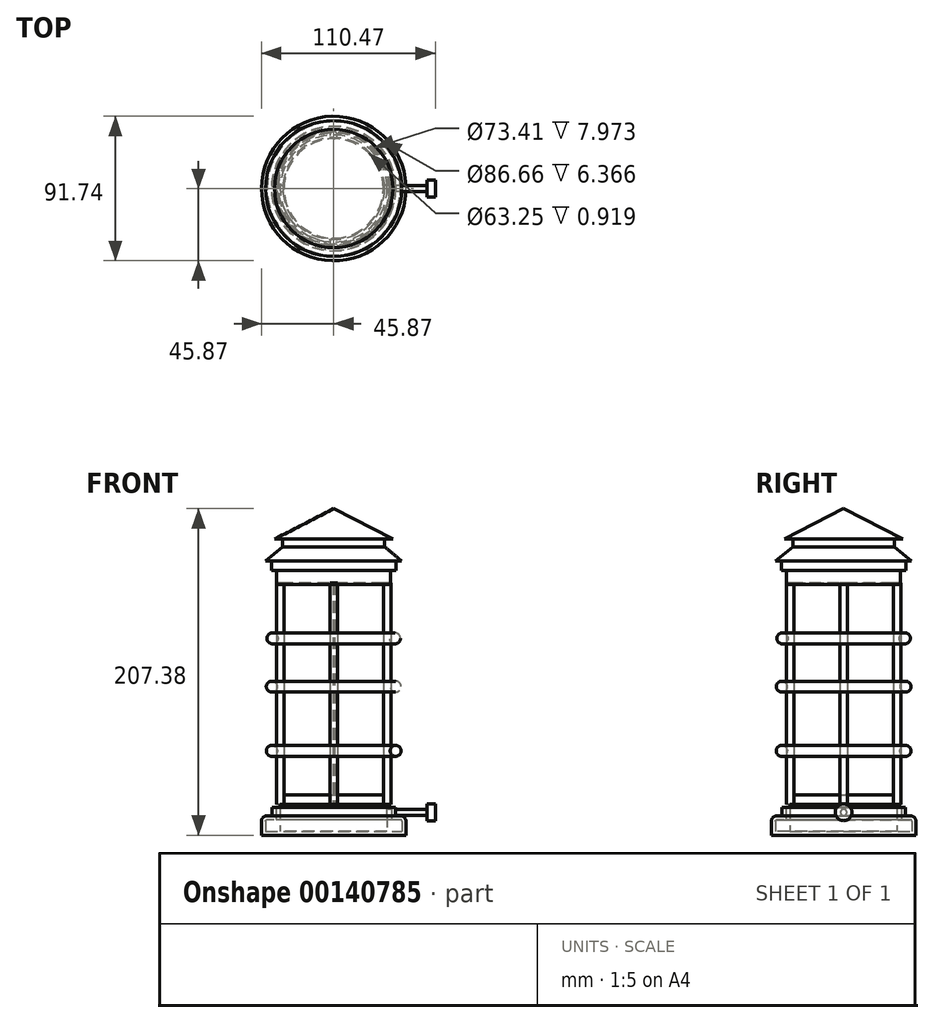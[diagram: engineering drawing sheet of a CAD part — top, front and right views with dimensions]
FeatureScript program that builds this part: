
annotation { "Feature Type Name" : "Feature", "Feature Type Description" : "" }
export const myFeature = defineFeature(function(context is Context, id is Id, definition is map)
    precondition{}
    {
        {
            var Q0;
            Q0=qCreatedBy(makeId("Front.planeOp"),FACE);
            var sketch = newSketch(context, id + "F0", { "sketchPlane" : qUnion([Q0])});
            skLineSegment(sketch, "E0", {"start": v(0, -64.78) * mm, "end": v(-52.83, -64.78) * mm});
            skLineSegment(sketch, "E1", {"start": v(-52.83, -64.78) * mm, "end": v(-45.18, -57.68) * mm});
            skLineSegment(sketch, "E2", {"start": v(-45.18, -57.68) * mm, "end": v(-45.18, -42.8) * mm});
            skLineSegment(sketch, "E3", {"start": v(-45.18, -42.8) * mm, "end": v(-47.57, -42.8) * mm});
            skLineSegment(sketch, "E4", {"start": v(-47.57, -42.8) * mm, "end": v(-47.57, -40.94) * mm});
            skLineSegment(sketch, "E5", {"start": v(-47.57, -40.94) * mm, "end": v(0, -40.94) * mm});
            skLineSegment(sketch, "E6", {"start": v(0, -40.94) * mm, "end": v(0, -64.78) * mm, "construction": true});
            skSolve(sketch);
        }
        {
            var Q0;
            Q0=sQuery(id+"F0.wireOp",EDGE,"E5");
            var Q1;
            Q1=sQuery(id+"F0.wireOp",EDGE,"E4");
            var Q2;
            Q2=sQuery(id+"F0.wireOp",EDGE,"E3");
            var Q3;
            Q3=sQuery(id+"F0.wireOp",EDGE,"E2");
            var Q4;
            Q4=sQuery(id+"F0.wireOp",EDGE,"E1");
            var Q5;
            Q5=sQuery(id+"F0.wireOp",EDGE,"E0");
            var Q6;
            Q6=sQuery(id+"F0.wireOp",EDGE,"E6");
            revolve(context, id + "F1", {"bodyType" : ToolBodyType.SURFACE, "surfaceEntities" : qUnion([Q0, Q1, Q2, Q3, Q4, Q5]), "axis" : qUnion([Q6]), "revolveType" : RevolveType.FULL});
        }
        {
            var Q0;
            Q0=makeQuery(id+"F1.opRevolve","SWEPT_FACE",FACE,{"disambiguationData":[OSD([sQuery(id+"F0.wireOp",EDGE,"E5")])]});
            var sketch = newSketch(context, id + "F2", { "sketchPlane" : qUnion([Q0])});
            skCircle(sketch, "E7", {"center": v(0, 0) * mm, "radius": 45.87 * mm});
            skSolve(sketch);
        }
        {
            var Q0;
            Q0=makeQuery(id+"F2.imprint","IMPRINT",FACE,{"disambiguationData":[TD([[makeQuery(id+"F2.imprint","IMPRINT",EDGE,{"derivedFrom":sQuery(id+"F2.wireOp",EDGE,"E7")}),1.0]])]});
            extrude(context, id + "F3", {"entities" : qUnion([Q0]), "depth" : 12.23 * mm});
        }
        {
            var Q0;
            Q0=makeQuery(id+"F3.opExtrude","CAP_EDGE",EDGE,{"disambiguationData":[OSD([sQuery(id+"F2.wireOp",EDGE,"E7")])],"isStart":false});
            fillet(context, id + "F4", {"entities" : qUnion([Q0]), "radius" : 3.32 * mm, "tangentPropagation" : true, "allowEdgeOverflow" : false});
        }
        {
            var Q0;
            Q0=makeQuery(id+"F3.opExtrude","CAP_FACE",FACE,{"disambiguationData":[OSD([sQuery(id+"F2.wireOp",EDGE,"E7")])],"isStart":false});
            var sketch = newSketch(context, id + "F5", { "sketchPlane" : qUnion([Q0])});
            skCircle(sketch, "E8", {"center": v(0, 0) * mm, "radius": 39.24 * mm});
            skSolve(sketch);
        }
        {
            var Q0;
            Q0=makeQuery(id+"F5.imprint","IMPRINT",FACE,{"disambiguationData":[TD([[makeQuery(id+"F5.imprint","IMPRINT",EDGE,{"derivedFrom":sQuery(id+"F5.wireOp",EDGE,"E8")}),1.0]])]});
            extrude(context, id + "F6", {"entities" : qUnion([Q0]), "operationType" : NewBodyOperationType.ADD, "depth" : 5.43 * mm});
        }
        {
            var Q0;
            Q0=makeQuery(id+"F6.opExtrude","CAP_FACE",FACE,{"disambiguationData":[OSD([sQuery(id+"F5.wireOp",EDGE,"E8")])],"isStart":false});
            shell(context, id + "F7", {"entities" : qUnion([Q0]), "thickness" : 2.54 * mm});
        }
        {
            var Q0;
            {var subQ0=sQuery(id+"F2.wireOp",EDGE,"E7");Q0=makeQuery(id+"F7.opShell","OFFSET_FACE",FACE,{"disambiguationData":[OSD([subQ0]),TDD([makeQuery(id+"F3.opExtrude","CAP_FACE",FACE,{"disambiguationData":[OSD([subQ0])],"isStart":true})])]});}
            var sketch = newSketch(context, id + "F8", { "sketchPlane" : qUnion([Q0])});
            skCircle(sketch, "E9", {"center": v(0, 0) * mm, "radius": 33.95 * mm});
            skSolve(sketch);
        }
        {
            var Q0;
            Q0 = qSketchRegion(id + "F8", true);
            extrude(context, id + "F9", {"entities" : qUnion([Q0]), "operationType" : NewBodyOperationType.ADD, "depth" : 17.16 * mm});
        }
        {
            var Q0;
            Q0=makeQuery(id+"F9.opExtrude","CAP_FACE",FACE,{"disambiguationData":[OSD([sQuery(id+"F8.wireOp",EDGE,"E9")])],"isStart":false});
            var sketch = newSketch(context, id + "F10", { "sketchPlane" : qUnion([Q0])});
            skCircle(sketch, "E10", {"center": v(0, 0) * mm, "radius": 31.65 * mm});
            skSolve(sketch);
        }
        {
            var Q0;
            Q0 = qSketchRegion(id + "F10", true);
            extrude(context, id + "F11", {"entities" : qUnion([Q0]), "operationType" : NewBodyOperationType.ADD, "depth" : 5.86 * mm});
        }
        {
            var Q0;
            Q0=makeQuery(id+"F9.opExtrude","CAP_FACE",FACE,{"disambiguationData":[OSD([sQuery(id+"F8.wireOp",EDGE,"E9")])],"isStart":false});
            var sketch = newSketch(context, id + "F12", { "sketchPlane" : qUnion([Q0])});
            skCircle(sketch, "E11", {"center": v(33.95, 0) * mm, "radius": 2.3 * mm});
            skCircle(sketch, "E12", {"center": v(-33.95, 0) * mm, "radius": 2.3 * mm});
            skCircle(sketch, "E13", {"center": v(0, 33.95) * mm, "radius": 2.3 * mm});
            skCircle(sketch, "E14", {"center": v(0, -33.95) * mm, "radius": 2.34 * mm});
            skSolve(sketch);
        }
        {
            var Q0;
            {var subQ0=sQuery(id+"F12.wireOp",EDGE,"E11");var subQ1=makeQuery(id+"F9.opExtrude","CAP_EDGE",EDGE,{"disambiguationData":[OSD([sQuery(id+"F8.wireOp",EDGE,"E9")])],"isStart":false});var subQ2=makeQuery(id+"F12.imprint","INTERSECT",VERTEX,{"disambiguationData":[OD(0.0)],"derivedFrom":[subQ1,subQ0]});Q0=makeQuery(id+"F12.imprint","IMPRINT",FACE,{"disambiguationData":[TD([[makeQuery(id+"F12.imprint","IMPRINT",EDGE,{"disambiguationData":[TD([[subQ2,1.0]])],"derivedFrom":subQ0}),1.0]])]});}
            var Q1;
            {var subQ0=sQuery(id+"F12.wireOp",EDGE,"E12");var subQ1=makeQuery(id+"F9.opExtrude","CAP_EDGE",EDGE,{"disambiguationData":[OSD([sQuery(id+"F8.wireOp",EDGE,"E9")])],"isStart":false});var subQ2=makeQuery(id+"F12.imprint","INTERSECT",VERTEX,{"disambiguationData":[OD(0.0)],"derivedFrom":[subQ1,subQ0]});Q1=makeQuery(id+"F12.imprint","IMPRINT",FACE,{"disambiguationData":[TD([[makeQuery(id+"F12.imprint","IMPRINT",EDGE,{"disambiguationData":[TD([[subQ2,1.0]])],"derivedFrom":subQ0}),1.0]])]});}
            var Q2;
            {var subQ0=sQuery(id+"F12.wireOp",EDGE,"E13");var subQ1=makeQuery(id+"F9.opExtrude","CAP_EDGE",EDGE,{"disambiguationData":[OSD([sQuery(id+"F8.wireOp",EDGE,"E9")])],"isStart":false});var subQ2=makeQuery(id+"F12.imprint","INTERSECT",VERTEX,{"disambiguationData":[OD(0.0)],"derivedFrom":[subQ1,subQ0]});Q2=makeQuery(id+"F12.imprint","IMPRINT",FACE,{"disambiguationData":[TD([[makeQuery(id+"F12.imprint","IMPRINT",EDGE,{"disambiguationData":[TD([[subQ2,1.0]])],"derivedFrom":subQ0}),1.0]])]});}
            var Q3;
            {var subQ0=sQuery(id+"F12.wireOp",EDGE,"E13");var subQ1=makeQuery(id+"F9.opExtrude","CAP_EDGE",EDGE,{"disambiguationData":[OSD([sQuery(id+"F8.wireOp",EDGE,"E9")])],"isStart":false});var subQ2=makeQuery(id+"F12.imprint","INTERSECT",VERTEX,{"disambiguationData":[OD(0.0)],"derivedFrom":[subQ1,subQ0]});Q3=makeQuery(id+"F12.imprint","IMPRINT",FACE,{"disambiguationData":[TD([[makeQuery(id+"F12.imprint","IMPRINT",EDGE,{"disambiguationData":[TD([[subQ2,-1.0]])],"derivedFrom":subQ0}),1.0]])]});}
            var Q4;
            {var subQ0=sQuery(id+"F12.wireOp",EDGE,"E12");var subQ1=makeQuery(id+"F9.opExtrude","CAP_EDGE",EDGE,{"disambiguationData":[OSD([sQuery(id+"F8.wireOp",EDGE,"E9")])],"isStart":false});var subQ2=makeQuery(id+"F12.imprint","INTERSECT",VERTEX,{"disambiguationData":[OD(0.0)],"derivedFrom":[subQ1,subQ0]});Q4=makeQuery(id+"F12.imprint","IMPRINT",FACE,{"disambiguationData":[TD([[makeQuery(id+"F12.imprint","IMPRINT",EDGE,{"disambiguationData":[TD([[subQ2,-1.0]])],"derivedFrom":subQ0}),1.0]])]});}
            var Q5;
            {var subQ0=sQuery(id+"F12.wireOp",EDGE,"E11");var subQ1=makeQuery(id+"F9.opExtrude","CAP_EDGE",EDGE,{"disambiguationData":[OSD([sQuery(id+"F8.wireOp",EDGE,"E9")])],"isStart":false});var subQ2=makeQuery(id+"F12.imprint","INTERSECT",VERTEX,{"disambiguationData":[OD(0.0)],"derivedFrom":[subQ1,subQ0]});Q5=makeQuery(id+"F12.imprint","IMPRINT",FACE,{"disambiguationData":[TD([[makeQuery(id+"F12.imprint","IMPRINT",EDGE,{"disambiguationData":[TD([[subQ2,-1.0]])],"derivedFrom":subQ0}),1.0]])]});}
            var Q6;
            {var subQ0=sQuery(id+"F12.wireOp",EDGE,"E14");var subQ1=makeQuery(id+"F9.opExtrude","CAP_EDGE",EDGE,{"disambiguationData":[OSD([sQuery(id+"F8.wireOp",EDGE,"E9")])],"isStart":false});var subQ2=makeQuery(id+"F12.imprint","INTERSECT",VERTEX,{"disambiguationData":[OD(0.0)],"derivedFrom":[subQ1,subQ0]});Q6=makeQuery(id+"F12.imprint","IMPRINT",FACE,{"disambiguationData":[TD([[makeQuery(id+"F12.imprint","IMPRINT",EDGE,{"disambiguationData":[TD([[subQ2,-1.0]])],"derivedFrom":subQ0}),1.0]])]});}
            var Q7;
            {var subQ0=sQuery(id+"F12.wireOp",EDGE,"E14");var subQ1=makeQuery(id+"F9.opExtrude","CAP_EDGE",EDGE,{"disambiguationData":[OSD([sQuery(id+"F8.wireOp",EDGE,"E9")])],"isStart":false});var subQ2=makeQuery(id+"F12.imprint","INTERSECT",VERTEX,{"disambiguationData":[OD(0.0)],"derivedFrom":[subQ1,subQ0]});Q7=makeQuery(id+"F12.imprint","IMPRINT",FACE,{"disambiguationData":[TD([[makeQuery(id+"F12.imprint","IMPRINT",EDGE,{"disambiguationData":[TD([[subQ2,1.0]])],"derivedFrom":subQ0}),1.0]])]});}
            extrude(context, id + "F13", {"entities" : qUnion([Q0, Q1, Q2, Q3, Q4, Q5, Q6, Q7]), "depth" : 140.45 * mm});
        }
        {
            var Q0;
            Q0=makeQuery(id+"F11.opExtrude","CAP_FACE",FACE,{"disambiguationData":[OSD([sQuery(id+"F10.wireOp",EDGE,"E10")])],"isStart":false});
            extrude(context, id + "F14", {"entities" : qUnion([Q0]), "depth" : 134.56 * mm});
        }
        {
            var Q0;
            Q0=makeQuery(id+"F14.opExtrude","CAP_FACE",FACE,{"disambiguationData":[OSD([sQuery(id+"F10.wireOp",EDGE,"E10")])],"isStart":false});
            shell(context, id + "F15", {"entities" : qUnion([Q0]), "thickness" : 0.03 * mm});
        }
        {
            var Q0;
            {var subQ0=sQuery(id+"F10.wireOp",EDGE,"E10");Q0=makeQuery(id+"F15.opShell","OFFSET_FACE",FACE,{"disambiguationData":[OSD([subQ0]),TDD([makeQuery(id+"F14.opExtrude","CAP_FACE",FACE,{"disambiguationData":[OSD([subQ0])],"isStart":true})])]});}
            extrude(context, id + "F16", {"entities" : qUnion([Q0]), "operationType" : NewBodyOperationType.ADD, "depth" : 133.61 * mm});
        }
        {
            var Q0;
            Q0=makeQuery(id+"F16.opExtrude","CAP_FACE",FACE,{"disambiguationData":[OSD([sQuery(id+"F10.wireOp",EDGE,"E10")])],"isStart":false});
            var sketch = newSketch(context, id + "F17", { "sketchPlane" : qUnion([Q0])});
            skCircle(sketch, "E15", {"center": v(0, 0) * mm, "radius": 36.18 * mm});
            skSolve(sketch);
        }
        {
            var Q0;
            Q0 = qSketchRegion(id + "F17", true);
            extrude(context, id + "F18", {"entities" : qUnion([Q0]), "depth" : 8.96 * mm});
        }
        {
            var Q0;
            Q0=makeQuery(id+"F18.opExtrude","CAP_FACE",FACE,{"disambiguationData":[OSD([sQuery(id+"F17.wireOp",EDGE,"E15")])],"isStart":false});
            var sketch = newSketch(context, id + "F19", { "sketchPlane" : qUnion([Q0])});
            skCircle(sketch, "E16", {"center": v(0, 0) * mm, "radius": 39.6 * mm});
            skSolve(sketch);
        }
        {
            var Q0;
            Q0=makeQuery(id+"F19.imprint","IMPRINT",FACE,{"disambiguationData":[TD([[makeQuery(id+"F19.imprint","IMPRINT",EDGE,{"derivedFrom":sQuery(id+"F19.wireOp",EDGE,"E16")}),1.0]])]});
            var Q1;
            Q1=makeQuery(id+"F19.imprint","IMPRINT",FACE,{"disambiguationData":[TD([[makeQuery(id+"F19.imprint","IMPRINT",EDGE,{"derivedFrom":makeQuery(id+"F18.opExtrude","CAP_EDGE",EDGE,{"disambiguationData":[OSD([sQuery(id+"F17.wireOp",EDGE,"E15")])],"isStart":false})}),1.0]])]});
            extrude(context, id + "F20", {"entities" : qUnion([Q0, Q1]), "operationType" : NewBodyOperationType.ADD, "depth" : 6.14 * mm});
        }
        {
            var Q0;
            Q0=makeQuery(id+"F20.opExtrude","CAP_FACE",FACE,{"disambiguationData":[OSD([sQuery(id+"F19.wireOp",EDGE,"E16")])],"isStart":false});
            var sketch = newSketch(context, id + "F21", { "sketchPlane" : qUnion([Q0])});
            skSolve(sketch);
        }
        {
            var Q0;
            Q0=makeQuery(id+"F21.imprint","IMPRINT",FACE,{"disambiguationData":[TD([[makeQuery(id+"F21.imprint","IMPRINT",EDGE,{"derivedFrom":makeQuery(id+"F20.opExtrude","CAP_EDGE",EDGE,{"disambiguationData":[OSD([sQuery(id+"F19.wireOp",EDGE,"E16")])],"isStart":false})}),1.0]])]});
            var sketch = newSketch(context, id + "F22", { "sketchPlane" : qUnion([Q0])});
            skSolve(sketch);
        }
        {
            var Q0;
            Q0=makeQuery(id+"F22.imprint","IMPRINT",FACE,{"disambiguationData":[TD([[makeQuery(id+"F22.imprint","IMPRINT",EDGE,{"derivedFrom":makeQuery(id+"F21.imprint","IMPRINT",EDGE,{"derivedFrom":makeQuery(id+"F20.opExtrude","CAP_EDGE",EDGE,{"disambiguationData":[OSD([sQuery(id+"F19.wireOp",EDGE,"E16")])],"isStart":false})})}),1.0]])]});
            var sketch = newSketch(context, id + "F23", { "sketchPlane" : qUnion([Q0])});
            skCircle(sketch, "E17", {"center": v(0, 0) * mm, "radius": 5.35 * mm});
            skSolve(sketch);
        }
        {
            var Q0;
            Q0=makeQuery(id+"F23.imprint","IMPRINT",FACE,{"disambiguationData":[TD([[makeQuery(id+"F23.imprint","IMPRINT",EDGE,{"derivedFrom":sQuery(id+"F23.wireOp",EDGE,"E17")}),1.0]])]});
            extrude(context, id + "F24", {"entities" : qUnion([Q0]), "operationType" : NewBodyOperationType.ADD, "depth" : 28.78 * mm});
        }
        {
            var Q0;
            Q0=qCreatedBy(makeId("Front.planeOp"),FACE);
            var sketch = newSketch(context, id + "F25", { "sketchPlane" : qUnion([Q0])});
            skLineSegment(sketch, "E18", {"start": v(0, 148) * mm, "end": v(0, 133.15) * mm});
            skLineSegment(sketch, "E19", {"start": v(0, 133.15) * mm, "end": v(43.2, 133.15) * mm});
            skLineSegment(sketch, "E20", {"start": v(43.2, 133.15) * mm, "end": v(32.35, 142.24) * mm});
            skLineSegment(sketch, "E21", {"start": v(32.35, 142.24) * mm, "end": v(32.35, 147.08) * mm});
            skLineSegment(sketch, "E22", {"start": v(32.35, 147.08) * mm, "end": v(37.62, 147.08) * mm});
            skLineSegment(sketch, "E23", {"start": v(37.62, 147.08) * mm, "end": v(0, 166.44) * mm});
            skLineSegment(sketch, "E24", {"start": v(0, 166.44) * mm, "end": v(0, 148) * mm});
            skSolve(sketch);
        }
        {
            var Q0;
            Q0=makeQuery(id+"F25.imprint","IMPRINT",FACE,{"disambiguationData":[TD([[makeQuery(id+"F25.imprint","IMPRINT",EDGE,{"derivedFrom":sQuery(id+"F25.wireOp",EDGE,"E18")}),1.0]])]});
            var Q1;
            Q1=sQuery(id+"F25.wireOp",EDGE,"E24");
            revolve(context, id + "F26", {"operationType" : NewBodyOperationType.ADD, "entities" : qUnion([Q0]), "axis" : qUnion([Q1]), "revolveType" : RevolveType.FULL});
        }
        {
            var Q0;
            Q0=qCreatedBy(makeId("Right.planeOp"),FACE);
            var sketch = newSketch(context, id + "F27", { "sketchPlane" : qUnion([Q0])});
            skCircle(sketch, "E25", {"center": v(-39.38, 53.45) * mm, "radius": 3.44 * mm});
            skCircle(sketch, "E26", {"center": v(-39.3, 12.6) * mm, "radius": 3.5 * mm});
            skCircle(sketch, "E27", {"center": v(-38.89, 84.08) * mm, "radius": 3.5 * mm});
            skSolve(sketch);
        }
        {
            var Q0;
            Q0=sQuery(id+"F27.wireOp",EDGE,"E25");
            var Q1;
            Q1=makeQuery(id+"F14.opExtrude","SWEPT_FACE",FACE,{"disambiguationData":[OSD([sQuery(id+"F10.wireOp",EDGE,"E10")])]});
            revolve(context, id + "F28", {"bodyType" : ToolBodyType.SURFACE, "surfaceEntities" : qUnion([Q0]), "axis" : qUnion([Q1]), "revolveType" : RevolveType.FULL});
        }
        {
            var Q0;
            Q0 = qSketchRegion(id + "F27", true);
            var Q1;
            Q1=makeQuery(id+"F14.opExtrude","SWEPT_FACE",FACE,{"disambiguationData":[OSD([sQuery(id+"F10.wireOp",EDGE,"E10")])]});
            revolve(context, id + "F29", {"entities" : qUnion([Q0]), "axis" : qUnion([Q1]), "revolveType" : RevolveType.FULL});
        }
        {
            var Q0;
            Q0 = qSketchRegion(id + "F27", true);
            var Q1;
            Q1=makeQuery(id+"F14.opExtrude","SWEPT_FACE",FACE,{"disambiguationData":[OSD([sQuery(id+"F10.wireOp",EDGE,"E10")])]});
            revolve(context, id + "F30", {"entities" : qUnion([Q0]), "axis" : qUnion([Q1]), "revolveType" : RevolveType.FULL});
        }
        {
            var Q0;
            Q0=qCreatedBy(makeId("Right.planeOp"),FACE);
            var sketch = newSketch(context, id + "F31", { "sketchPlane" : qUnion([Q0])});
            skCircle(sketch, "E28", {"center": v(0, -26.4) * mm, "radius": 1.99 * mm});
            skSolve(sketch);
        }
        {
            var Q0;
            Q0 = qSketchRegion(id + "F31", true);
            extrude(context, id + "F32", {"entities" : qUnion([Q0]), "operationType" : NewBodyOperationType.ADD, "depth" : 64.6 * mm});
        }
        {
            var Q0;
            Q0=makeQuery(id+"F32.opExtrude","CAP_FACE",FACE,{"disambiguationData":[OSD([sQuery(id+"F31.wireOp",EDGE,"E28")])],"isStart":false});
            var sketch = newSketch(context, id + "F33", { "sketchPlane" : qUnion([Q0])});
            skCircle(sketch, "E29", {"center": v(0, -26.4) * mm, "radius": 5.31 * mm});
            skSolve(sketch);
        }
        {
            var Q0;
            Q0=makeQuery(id+"F33.imprint","IMPRINT",FACE,{"disambiguationData":[TD([[makeQuery(id+"F33.imprint","IMPRINT",EDGE,{"derivedFrom":sQuery(id+"F33.wireOp",EDGE,"E29")}),1.0]])]});
            var Q1;
            Q1=makeQuery(id+"F33.imprint","IMPRINT",FACE,{"disambiguationData":[TD([[makeQuery(id+"F33.imprint","IMPRINT",EDGE,{"derivedFrom":makeQuery(id+"F32.opExtrude","CAP_EDGE",EDGE,{"disambiguationData":[OSD([sQuery(id+"F31.wireOp",EDGE,"E28")])],"isStart":false})}),1.0]])]});
            extrude(context, id + "F34", {"entities" : qUnion([Q0, Q1]), "operationType" : NewBodyOperationType.ADD, "oppositeDirection" : true, "depth" : 5.38 * mm});
        }
    });
